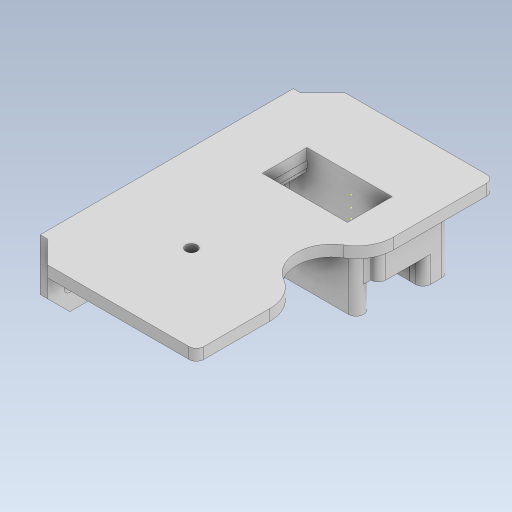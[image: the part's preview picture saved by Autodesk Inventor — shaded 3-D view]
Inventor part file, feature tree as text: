
AUTODESK INVENTOR PART (.ipt)
format: ipt  version: 2023.5 (Build 275446000, 446)  size: 536,576 bytes
history: native  units: mm
features: extrude x14, sketch x9, fillet x4, chamfer x2
ambient origin geometry x8: Origin, YZ Plane, XZ Plane, XY Plane, X Axis, Y Axis, Z Axis, Center Point
bodies: Body1 (feature_tree)
feature tree (29):
  extrude  "Extrusion3"  Depth=2.0mm TaperAngle=0.0deg
  extrude  "Extrusion4"  Depth=12.0mm TaperAngle=0.0deg
  extrude  "Extrusion5"  Depth=4.0mm TaperAngle=0.0deg
  extrude  "Extrusion9"  Depth=50.0mm
  extrude  "Extrusion10"  Depth=3.0mm TaperAngle=0.0deg
  extrude  "Extrusion11"  Depth=3.0mm TaperAngle=0.0deg
  extrude  "Extrusion12"  Depth=2.0mm TaperAngle=0.0deg
  fillet  "Fillet1"  Radius=2.0mm
  fillet  "Fillet2"  Radius=2.0mm
  chamfer  "Chamfer4"  Distance=2.0mm Angle=45.0deg
  extrude  "Extrusion13"  Depth=23.2mm
  extrude  "Extrusion14"  Depth=10.0mm TaperAngle=0.0deg
  chamfer  "Chamfer5"  Distance=2.0mm
  extrude  "Extrusion15"  Depth=2.0mm TaperAngle=45.0deg
  extrude  "Extrusion16"  Depth=2.0mm
  fillet  "Fillet3"  Radius=2.4mm
  extrude  "Extrusion17"  Depth=10.0mm
  fillet  "Fillet4"  Radius=4.0mm
  extrude  "Extrusion18"  Depth=10.0mm TaperAngle=0.0deg
  extrude  "Extrusion19"  Depth=10.0mm
  sketch  "Sketch3"  dims[d4=2.0mm d5=14.25mm d6=0.0mm]
  sketch  "Sketch6"  dims[d7=35.0mm d8=12.0mm d9=0.0mm]
  sketch  "Sketch15"  dims[d10=15.0mm d11=4.0mm d12=0.0mm]
  sketch  "Sketch18"  dims[d33=11.005905mm d34=50.0mm]
  sketch  "Sketch24"  dims[d35=80.0mm d36=3.0mm d37=0.0mm]
  sketch  "Sketch26"  dims[d38=5.8mm d39=3.0mm d40=0.0mm]
  sketch  "Sketch27"  dims[d41=6.0mm d42=0.0mm d43=7.0mm d44=0.0mm d45=2.0mm d46=2.0mm d47=6.0mm d48=2.0mm d49=45.0deg]
  sketch  "Sketch28"  dims[d50=3.0mm d51=23.2mm]
  sketch  "Sketch29"  dims[d52=21.45mm d53=4.0mm d54=0.0mm d55=2.0mm d56=0.0mm d57=6.0mm d58=2.0mm d59=45.0deg d60=2.0mm d61=2.4mm d62=6.2mm d63=4.0mm d64=0.0mm d65=4.0mm d66=0.0mm d67=6.0mm d68=2.152328mm d69=2.0mm d70=10.0mm d71=0.0mm d72=10.0mm d73=3.0mm d74=3.0mm d75=10.0mm d76=0.0mm d77=3.0mm d78=3.0mm d79=10.0mm d80=10.0mm d81=0.0mm d26=0.5mm d27=0.872665mm d28=0.5mm d29=0.872665mm d30=0.5mm d31=0.872665mm]
